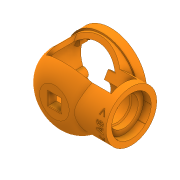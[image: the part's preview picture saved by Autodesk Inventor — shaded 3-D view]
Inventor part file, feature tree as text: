
AUTODESK INVENTOR PART (.ipt)
format: ipt  version: 2020 (Build 240168000, 168)  size: 938,496 bytes
history: native  units: in
note: dims shown in document units (in); Inventor stores cm internally (conversion verified against a paired STEP export)
features: sketch x28, extrude x25, projected_geometry x15, plane x8, chamfer x6, fillet x2, revolve x1, emboss x1
ambient origin geometry x8: Origin, YZ Plane, XZ Plane, XY Plane, X Axis, Y Axis, Z Axis, Center Point
bodies: Solid1 (feature_tree)
feature tree (86):
  extrude  "Extrusion1"  Depth=0.315in TaperAngle=0.0deg
  chamfer  "Chamfer1"  Distance=0.315in
  extrude  "Extrusion2"  Depth=2.3622in TaperAngle=360.0deg
  extrude  "Extrusion3"  Depth=0.315in TaperAngle=0.0deg
  extrude  "Extrusion4"  Depth=0.1575in TaperAngle=0.0deg
  extrude  "Extrusion5"  Depth=0.1575in TaperAngle=0.0deg
  revolve  "Revolution1"  [1 undecoded]
  plane  "Work Plane1"
  extrude  "Extrusion6"  Depth=0.1575in
  plane  "Work Plane2"
  plane  "Work Plane3"
  extrude  "Extrusion8"  [1 undecoded]
  extrude  "Extrusion9"  Depth=0.1575in TaperAngle=0.0deg
  chamfer  "Chamfer3"  Distance=1.8898in
  extrude  "Extrusion10"  Depth=1.8898in
  plane  "Work Plane4"
  extrude  "Extrusion11"  Depth=0.315in TaperAngle=0.0deg
  extrude  "Extrusion12"  Depth=0.2756in
  extrude  "Extrusion13"  Depth=3.1496in TaperAngle=360.0deg
  plane  "Work Plane5"
  extrude  "Extrusion15"  [1 undecoded]
  extrude  "Extrusion16"  Depth=0.4764in
  plane  "Work Plane6"
  extrude  "Extrusion18"  Depth=0.315in
  extrude  "Extrusion20"  Depth=0.315in
  extrude  "Extrusion21"  TaperAngle=60.0deg  [1 undecoded]
  extrude  "Extrusion22"  TaperAngle=0.0deg  [1 undecoded]
  chamfer  "Chamfer34"  Distance=2.3622in
  chamfer  "Chamfer35"  Distance=0.1969in
  fillet  "Fillet1"  [1 undecoded]
  plane  "Work Plane7"
  emboss  "Emboss1"
  chamfer  "Chamfer36"  Distance=0.1969in
  sketch  "Sketch25"  dims[d178=0.315in]
  plane  "Work Plane8"
  extrude  "Extrusion23"  Depth=0.0984in TaperAngle=0.0deg
  extrude  "Extrusion24"  Depth=0.0984in TaperAngle=0.0deg
  extrude  "Extrusion25"  Depth=0.0984in
  extrude  "Extrusion26"  Depth=0.315in
  extrude  "Extrusion27"  Depth=0.315in TaperAngle=0.0deg
  fillet  "Fillet3"  Radius=0.0787in
  extrude  "Extrusion29"  Depth=0.315in
  chamfer  "Chamfer37"  [1 undecoded]
  extrude  "Extrusion30"  Depth=0.315in TaperAngle=0.0deg
  sketch  "Sketch1"  dims[d0=0.4724in d1=0.315in d2=0.0in d3=0.315in d4=0.125in d5=0.0137in]
  sketch  "Sketch2"  dims[d6=0.0157in d7=2.3622in d9=360.0deg]
  sketch  "Sketch3"  dims[d11=0.315in d12=0.0in d13=0.0197in d14=0.0in]
  projected_geometry  "Projected Loop1"
  sketch  "Sketch4"  dims[d15=2.5591in d16=0.1575in d17=0.0in]
  sketch  "Sketch5"  dims[d18=0.1575in d19=1.2598in d20=0.0in]
  sketch  "Sketch6"  dims[d21=1.1024in d22=0.5512in]
  sketch  "Sketch7"  dims[d23=0.8465in d24=0.1575in]
  sketch  "Sketch9"  dims[d25=90.0deg d26=-2.1063in]
  sketch  "Sketch10"  dims[d27=0.1575in d28=0.1575in d29=0.0in d33=-0.1575in d41=1.8898in]
  sketch  "Sketch11"  dims[d42=1.2795in d43=1.8898in]
  sketch  "Sketch12"  dims[d44=0.2165in d45=0.315in d46=0.0in]
  sketch  "Sketch13"  dims[d47=1.1811in d48=0.0in d49=0.2756in d50=0.125in d51=0.0137in]
  sketch  "Sketch14"  dims[d52=0.0157in d53=3.1496in d55=360.0deg]
  sketch  "Sketch16"  dims[d57=0.2756in d58=0.0in d59=-0.2756in]
  sketch  "Sketch17"  dims[d61=0.9843in d62=0.0in d63=0.4764in]
  sketch  "Sketch19"  dims[d64=0.315in d65=0.0in d66=0.0787in]
  projected_geometry  "Projected Loop2"
  projected_geometry  "Projected Loop3"
  sketch  "Sketch21"  dims[d73=0.315in d74=0.0in d166=0.9843in]
  sketch  "Sketch22"  dims[d171=-0.2756in d172=60.0deg]
  sketch  "Sketch23"  dims[d173=60.0deg d174=0.0in]
  projected_geometry  "Projected Loop4"
  sketch  "Sketch24"  dims[d175=0.0in d176=2.3622in d177=0.0in]
  sketch  "Sketch28"  dims[d179=0.2067in]
  sketch  "Sketch29"  dims[d180=0.0787in]
  sketch  "Sketch30"  dims[d181=45.0deg d182=0.1969in d183=0.0in d187=-0.4921in d188=0.1969in d189=0.0in]
  projected_geometry  "Projected Loop5"
  sketch  "Sketch31"  dims[d193=0.315in d194=0.0984in d195=0.0in]
  sketch  "Sketch32"  dims[d196=0.2362in d197=0.0984in d198=0.0in]
  sketch  "Sketch34"  dims[d199=0.0984in d200=0.0in d201=0.0591in d202=0.125in d203=0.0137in]
  sketch  "Sketch35"  dims[d204=0.0591in d205=0.125in d206=0.0137in d207=0.0197in d209=0.0394in d210=0.0in d211=0.0787in d212=0.125in d213=0.0137in d214=2.126in d215=-0.1575in d217=0.4921in d218=0.0in d220=4.7244in d221=0.1083in d222=0.1575in d223=360.0deg d224=0.1969in d225=0.1969in d226=0.1969in d227=0.1969in d228=0.1969in d229=0.1969in d230=0.1969in d231=0.1969in d232=0.1969in d233=0.1969in d234=0.0787in d235=0.0787in d236=0.0787in d237=0.0787in d238=0.0787in d239=0.0787in d240=0.0787in d241=0.0787in d242=0.0787in d243=0.0787in d244=0.315in d245=0.0in d246=0.315in d247=0.0in d248=0.0591in d249=0.315in d250=0.0in d251=0.0394in d252=0.0in d253=0.4803in d254=0.4803in d257=0.0197in d258=0.0394in d259=0.2362in d260=0.0in d261=0.0394in d262=0.125in d263=45.0deg d264=0.1181in d265=0.0in d266=0.5in d267=0.0344in]
  projected_geometry  "Projected Loop7"
  projected_geometry  "Projected Loop8"
  projected_geometry  "Projected Loop9"
  projected_geometry  "Projected Loop10"
  projected_geometry  "Projected Loop11"
  projected_geometry  "Projected Loop12"
  projected_geometry  "Projected Loop13"
  projected_geometry  "Projected Loop14"
  projected_geometry  "Projected Loop15"
  projected_geometry  "Projected Loop16"
note: 7 required parameter values undecoded (feature->parameter linkage not recoverable at this tier; creation-order binding heuristic only, values carry confidence <= 0.55)